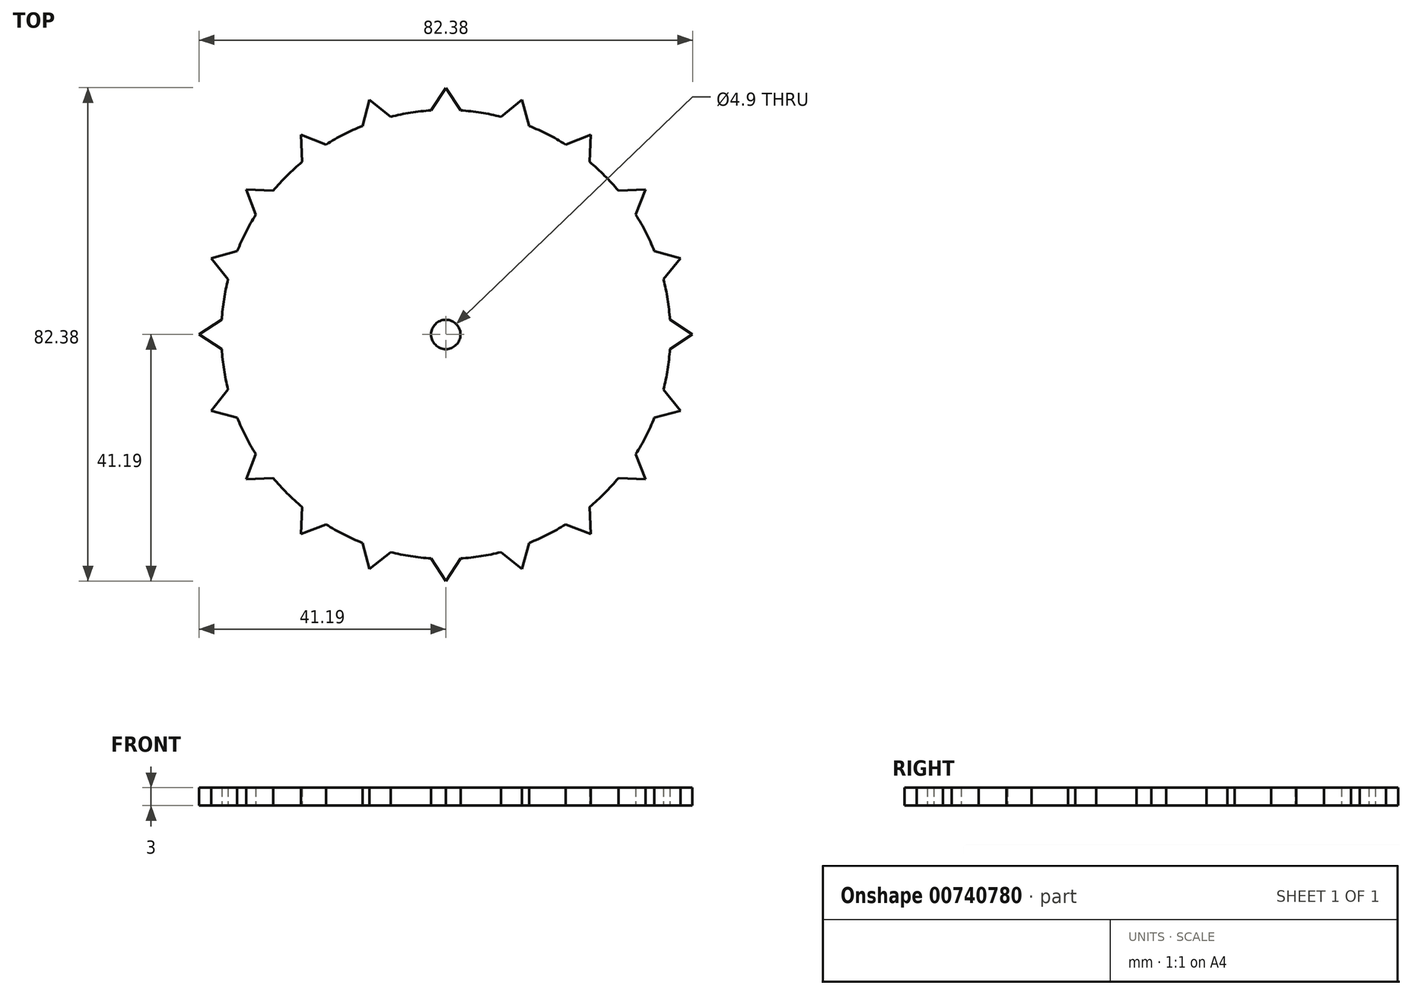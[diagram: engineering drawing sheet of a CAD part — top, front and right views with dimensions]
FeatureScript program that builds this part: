
annotation { "Feature Type Name" : "Feature", "Feature Type Description" : "" }
export const myFeature = defineFeature(function(context is Context, id is Id, definition is map)
    precondition{}
    {
        {
            var Q0;
            Q0=qCreatedBy(makeId("Top.planeOp"),FACE);
            var sketch = newSketch(context, id + "F0", { "sketchPlane" : qUnion([Q0])});
            skCircle(sketch, "E0", {"center": v(0, 0) * mm, "radius": 37.5 * mm});
            skLineSegment(sketch, "E1", {"start": v(-2.47, 37.42) * mm, "end": v(0, 41.19) * mm});
            skLineSegment(sketch, "E2", {"start": v(0, 41.19) * mm, "end": v(2.47, 37.42) * mm});
            skLineSegment(sketch, "E3.1.0", {"start": v(-12.73, 39.17) * mm, "end": v(-9.22, 36.35) * mm});
            skLineSegment(sketch, "E3.1.1", {"start": v(-13.9, 34.83) * mm, "end": v(-12.73, 39.17) * mm});
            skLineSegment(sketch, "E3.2.0", {"start": v(-24.2, 33.32) * mm, "end": v(-20, 31.72) * mm});
            skLineSegment(sketch, "E3.2.1", {"start": v(-23.99, 28.82) * mm, "end": v(-24.2, 33.32) * mm});
            skLineSegment(sketch, "E3.3.0", {"start": v(-33.32, 24.2) * mm, "end": v(-28.82, 23.99) * mm});
            skLineSegment(sketch, "E3.3.1", {"start": v(-31.72, 20) * mm, "end": v(-33.32, 24.2) * mm});
            skLineSegment(sketch, "E3.4.0", {"start": v(-39.17, 12.73) * mm, "end": v(-34.83, 13.9) * mm});
            skLineSegment(sketch, "E3.4.1", {"start": v(-36.35, 9.22) * mm, "end": v(-39.17, 12.73) * mm});
            skLineSegment(sketch, "E3.5.0", {"start": v(-41.19, 0) * mm, "end": v(-37.42, 2.47) * mm});
            skLineSegment(sketch, "E3.5.1", {"start": v(-37.42, -2.47) * mm, "end": v(-41.19, 0) * mm});
            skLineSegment(sketch, "E3.6.0", {"start": v(-39.17, -12.73) * mm, "end": v(-36.35, -9.22) * mm});
            skLineSegment(sketch, "E3.6.1", {"start": v(-34.83, -13.9) * mm, "end": v(-39.17, -12.73) * mm});
            skLineSegment(sketch, "E3.7.0", {"start": v(-33.32, -24.2) * mm, "end": v(-31.72, -20) * mm});
            skLineSegment(sketch, "E3.7.1", {"start": v(-28.82, -23.99) * mm, "end": v(-33.32, -24.2) * mm});
            skLineSegment(sketch, "E3.8.0", {"start": v(-24.2, -33.32) * mm, "end": v(-23.99, -28.82) * mm});
            skLineSegment(sketch, "E3.8.1", {"start": v(-20, -31.72) * mm, "end": v(-24.2, -33.32) * mm});
            skLineSegment(sketch, "E3.9.0", {"start": v(-12.73, -39.17) * mm, "end": v(-13.9, -34.83) * mm});
            skLineSegment(sketch, "E3.9.1", {"start": v(-9.22, -36.35) * mm, "end": v(-12.73, -39.17) * mm});
            skLineSegment(sketch, "E3.10.0", {"start": v(0, -41.19) * mm, "end": v(-2.47, -37.42) * mm});
            skLineSegment(sketch, "E3.10.1", {"start": v(2.47, -37.42) * mm, "end": v(0, -41.19) * mm});
            skLineSegment(sketch, "E3.11.0", {"start": v(12.73, -39.17) * mm, "end": v(9.22, -36.35) * mm});
            skLineSegment(sketch, "E3.11.1", {"start": v(13.9, -34.83) * mm, "end": v(12.73, -39.17) * mm});
            skLineSegment(sketch, "E3.12.0", {"start": v(24.2, -33.32) * mm, "end": v(20, -31.72) * mm});
            skLineSegment(sketch, "E3.12.1", {"start": v(23.99, -28.82) * mm, "end": v(24.2, -33.32) * mm});
            skLineSegment(sketch, "E3.13.0", {"start": v(33.32, -24.2) * mm, "end": v(28.82, -23.99) * mm});
            skLineSegment(sketch, "E3.13.1", {"start": v(31.72, -20) * mm, "end": v(33.32, -24.2) * mm});
            skLineSegment(sketch, "E3.14.0", {"start": v(39.17, -12.73) * mm, "end": v(34.83, -13.9) * mm});
            skLineSegment(sketch, "E3.14.1", {"start": v(36.35, -9.22) * mm, "end": v(39.17, -12.73) * mm});
            skLineSegment(sketch, "E3.15.0", {"start": v(41.19, 0) * mm, "end": v(37.42, -2.47) * mm});
            skLineSegment(sketch, "E3.15.1", {"start": v(37.42, 2.47) * mm, "end": v(41.19, 0) * mm});
            skLineSegment(sketch, "E3.16.0", {"start": v(39.17, 12.73) * mm, "end": v(36.35, 9.22) * mm});
            skLineSegment(sketch, "E3.16.1", {"start": v(34.83, 13.9) * mm, "end": v(39.17, 12.73) * mm});
            skLineSegment(sketch, "E3.17.0", {"start": v(33.32, 24.2) * mm, "end": v(31.72, 20) * mm});
            skLineSegment(sketch, "E3.17.1", {"start": v(28.82, 23.99) * mm, "end": v(33.32, 24.2) * mm});
            skLineSegment(sketch, "E3.18.0", {"start": v(24.2, 33.32) * mm, "end": v(23.99, 28.82) * mm});
            skLineSegment(sketch, "E3.18.1", {"start": v(20, 31.72) * mm, "end": v(24.2, 33.32) * mm});
            skLineSegment(sketch, "E3.19.0", {"start": v(12.73, 39.17) * mm, "end": v(13.9, 34.83) * mm});
            skLineSegment(sketch, "E3.19.1", {"start": v(9.22, 36.35) * mm, "end": v(12.73, 39.17) * mm});
            skSolve(sketch);
        }
        {
            var Q0;
            Q0=qSketchRegion(id+"F0",true);
            extrude(context, id + "F1", {"entities" : qUnion([Q0]), "depth" : 3 * mm, "offsetDistance" : 25 * mm});
        }
        {
            var Q0;
            Q0=makeQuery(id+"F1.opExtrude","CAP_FACE",FACE,{"disambiguationData":[OSD([sQuery(id+"F0.wireOp",EDGE,"E0"),sQuery(id+"F0.wireOp",EDGE,"E1"),sQuery(id+"F0.wireOp",EDGE,"E2"),sQuery(id+"F0.wireOp",EDGE,"E3.1.0"),sQuery(id+"F0.wireOp",EDGE,"E3.1.1"),sQuery(id+"F0.wireOp",EDGE,"E3.2.0"),sQuery(id+"F0.wireOp",EDGE,"E3.2.1"),sQuery(id+"F0.wireOp",EDGE,"E3.3.0"),sQuery(id+"F0.wireOp",EDGE,"E3.3.1"),sQuery(id+"F0.wireOp",EDGE,"E3.4.0"),sQuery(id+"F0.wireOp",EDGE,"E3.4.1"),sQuery(id+"F0.wireOp",EDGE,"E3.5.0"),sQuery(id+"F0.wireOp",EDGE,"E3.5.1"),sQuery(id+"F0.wireOp",EDGE,"E3.6.0"),sQuery(id+"F0.wireOp",EDGE,"E3.6.1"),sQuery(id+"F0.wireOp",EDGE,"E3.7.0"),sQuery(id+"F0.wireOp",EDGE,"E3.7.1"),sQuery(id+"F0.wireOp",EDGE,"E3.8.0"),sQuery(id+"F0.wireOp",EDGE,"E3.8.1"),sQuery(id+"F0.wireOp",EDGE,"E3.9.0"),sQuery(id+"F0.wireOp",EDGE,"E3.9.1"),sQuery(id+"F0.wireOp",EDGE,"E3.10.0"),sQuery(id+"F0.wireOp",EDGE,"E3.10.1"),sQuery(id+"F0.wireOp",EDGE,"E3.11.0"),sQuery(id+"F0.wireOp",EDGE,"E3.11.1"),sQuery(id+"F0.wireOp",EDGE,"E3.12.0"),sQuery(id+"F0.wireOp",EDGE,"E3.12.1"),sQuery(id+"F0.wireOp",EDGE,"E3.13.0"),sQuery(id+"F0.wireOp",EDGE,"E3.13.1"),sQuery(id+"F0.wireOp",EDGE,"E3.14.0"),sQuery(id+"F0.wireOp",EDGE,"E3.14.1"),sQuery(id+"F0.wireOp",EDGE,"E3.15.0"),sQuery(id+"F0.wireOp",EDGE,"E3.15.1"),sQuery(id+"F0.wireOp",EDGE,"E3.16.0"),sQuery(id+"F0.wireOp",EDGE,"E3.16.1"),sQuery(id+"F0.wireOp",EDGE,"E3.17.0"),sQuery(id+"F0.wireOp",EDGE,"E3.17.1"),sQuery(id+"F0.wireOp",EDGE,"E3.18.0"),sQuery(id+"F0.wireOp",EDGE,"E3.18.1"),sQuery(id+"F0.wireOp",EDGE,"E3.19.0"),sQuery(id+"F0.wireOp",EDGE,"E3.19.1")])],"isStart":false});
            var sketch = newSketch(context, id + "F2", { "sketchPlane" : qUnion([Q0])});
            skCircle(sketch, "E4", {"center": v(0, 0) * mm, "radius": 2.45 * mm});
            skSolve(sketch);
        }
        {
            var Q0;
            Q0=makeQuery(id+"F2.imprint","IMPRINT",FACE,{"disambiguationData":[TD([[makeQuery(id+"F2.imprint","IMPRINT",EDGE,{"derivedFrom":sQuery(id+"F2.wireOp",EDGE,"E4")}),1.0]])]});
            extrude(context, id + "F3", {"entities" : qUnion([Q0]), "operationType" : NewBodyOperationType.REMOVE, "oppositeDirection" : true, "depth" : 3 * mm, "offsetDistance" : 25 * mm});
        }
    });
